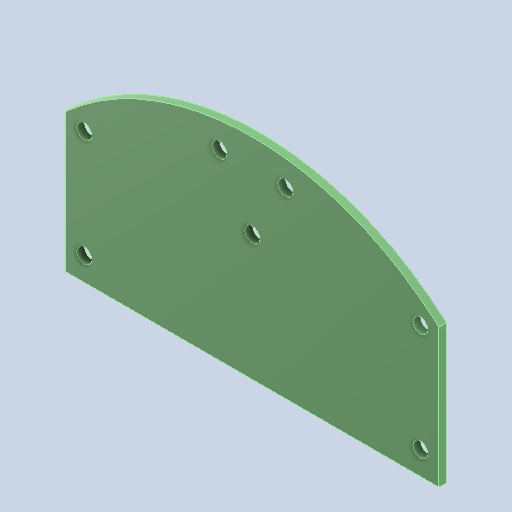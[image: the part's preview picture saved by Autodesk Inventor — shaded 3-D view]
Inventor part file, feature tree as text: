
AUTODESK INVENTOR PART (.ipt)
format: ipt  version: 2025.3 (Build 293356030, 356C)  size: 151,552 bytes
history: native  units: mm
features: sketch x3, other x2, hole x2, extrude x1
ambient origin geometry x8: Origin, YZ Plane, XZ Plane, XY Plane, X Axis, Y Axis, Z Axis, Center Point
bodies: Body1 (feature_tree)
feature tree (8):
  other  "BaseBoard-SPG27.ipt"
  other  "ソリッド1"
  extrude  "基板"  Depth=120.0mm
  hole  "ボールキャスター取付穴"  [1 undecoded]
  hole  "連結穴"  [1 undecoded]
  sketch  "スケッチ1"
  sketch  "スケッチ3"
  sketch  "スケッチ5"
note: 2 required parameter values undecoded (feature->parameter linkage not recoverable at this tier; creation-order binding heuristic only, values carry confidence <= 0.55)
